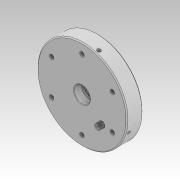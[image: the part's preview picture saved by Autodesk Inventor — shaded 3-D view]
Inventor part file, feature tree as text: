
AUTODESK INVENTOR PART (.ipt)
format: ipt  version: 2020 (Build 240168000, 168)  size: 842,752 bytes
history: native  units: mm
features: sketch x14, extrude x12, plane x3, pattern_circular x2, chamfer x2, fillet x2, revolve x1, projected_geometry x1
ambient origin geometry x8: Origin, YZ Plane, XZ Plane, XY Plane, X Axis, Y Axis, Z Axis, Center Point
bodies: Solid1 (feature_tree)
feature tree (37):
  extrude  "Extrusion1"  Depth=90.0mm
  extrude  "Extrusion6"  TaperAngle=0.0deg  [1 undecoded]
  extrude  "Extrusion5"  Depth=7.5mm TaperAngle=0.0deg
  pattern_circular  "Circular Pattern2"  Count=6 Angle=360.0deg
  extrude  "Extrusion7"  Depth=5.6mm
  extrude  "Extrusion8"  Depth=60.0mm TaperAngle=360.0deg
  pattern_circular  "Circular Pattern1"  [2 undecoded]
  extrude  "Extrusion11"  Depth=1.0mm TaperAngle=0.0deg
  extrude  "Extrusion12"  TaperAngle=90.0deg  [1 undecoded]
  extrude  "Extrusion13"  Depth=1.0mm
  plane  "Work Plane1"
  sketch  "Sketch13"  dims[d44=3.0mm]
  plane  "Work Plane2"
  plane  "Work Plane3"
  extrude  "Extrusion14"  Depth=1.0mm
  extrude  "Extrusion15"  Depth=1.0mm TaperAngle=45.0deg
  chamfer  "Chamfer1"  Angle=45.0deg  [1 undecoded]
  fillet  "Fillet1"  Radius=2.0mm
  revolve  "Revolution1"  [1 undecoded]
  fillet  "Fillet2"  Radius=200.0mm
  chamfer  "Chamfer2"  Distance=1.308997mm
  extrude  "Extrusion16"  Depth=1.0mm
  extrude  "Extrusion17"  Depth=1.0mm
  sketch  "Sketch1"  dims[d0=12.6mm d1=90.0mm]
  sketch  "Sketch4"  dims[d2=16.0mm d3=0.0mm d20=0.0mm d21=0.0mm]
  sketch  "Sketch5"  dims[d22=16.0mm d23=7.5mm d24=0.0mm]
  sketch  "Sketch6"  dims[d25=3.5mm]
  sketch  "Sketch7"  dims[d26=35.0mm d27=60.0mm d29=360.0deg]
  sketch  "Sketch10"  dims[d31=0.0mm d32=0.0mm d33=5.6mm]
  sketch  "Sketch11"  dims[d34=4.0mm d35=0.0mm d40=60.0mm d41=360.0deg]
  sketch  "Sketch12"  dims[d43=25.0mm]
  sketch  "Sketch14"  dims[d45=7.0mm d46=0.0mm]
  sketch  "Sketch15"  dims[d47=4.0mm d48=0.0mm]
  projected_geometry  "Projected Loop1"
  sketch  "Sketch16"  dims[d50=4.0mm d51=0.0mm]
  sketch  "Sketch17"  dims[d52=3.5mm]
  sketch  "Sketch18"  dims[d53=7.5mm d54=0.0mm d55=3.0mm d56=7.5mm d57=0.0mm d58=90.0deg d59=50.0mm d60=2.96706mm d61=1.0mm d62=2.0mm d63=45.0deg d64=45.0deg d65=2.0mm d66=0.75mm d67=10.9mm d68=12.6mm d69=200.0mm d70=360.0deg d72=1.308997mm d73=5.0mm d75=6.0mm d76=2.5mm d77=30.0deg d78=3.0mm d79=90.0deg d80=0.3mm d81=0.5mm d82=2.0mm d83=45.0deg d84=59.0mm d85=86.0mm d86=1.0mm d87=0.0mm d88=4.0mm d89=0.0mm]
note: 6 required parameter values undecoded (feature->parameter linkage not recoverable at this tier; creation-order binding heuristic only, values carry confidence <= 0.55)